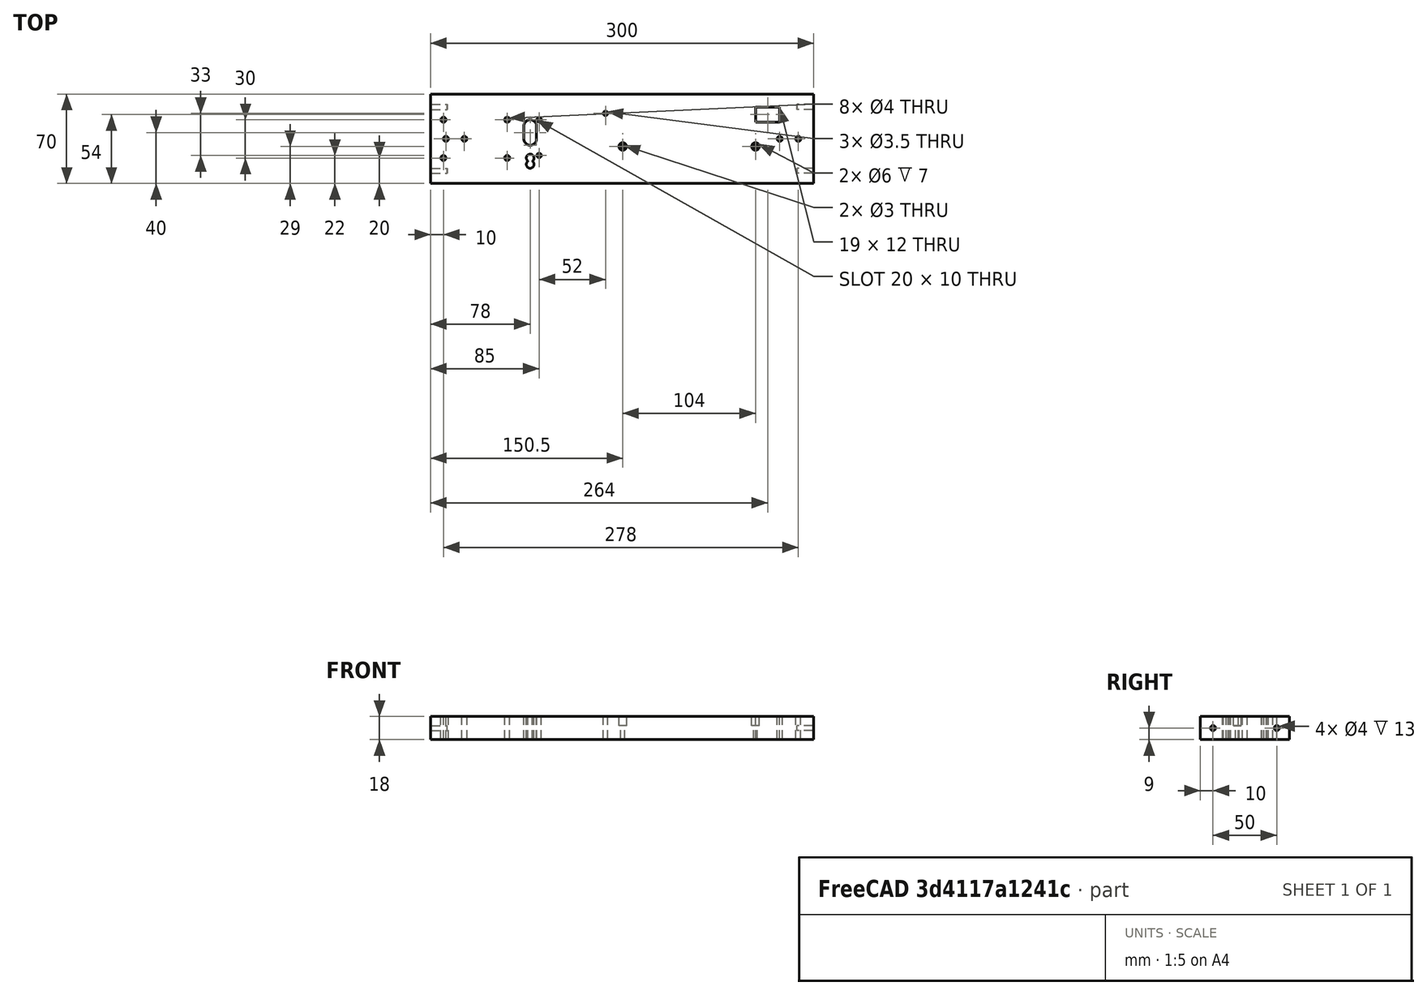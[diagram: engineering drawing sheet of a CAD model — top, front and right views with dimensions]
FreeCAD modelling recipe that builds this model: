
FCSTD DOCUMENT  (FreeCAD 0.17R13541 (Git))
Label: BaseLateralIzquierda
License: All rights reserved
LicenseURL: http://en.wikipedia.org/wiki/All_rights_reserved
objects: Part::Cylinder×21, Part::Cut×13, Part::Box×3, Part::MultiFuse×3, Part::Mirroring×2
note: 42 computed .brp shape members not serialized (recipe doc carries the construction recipe); baked Part::Feature solids carry a one-line shape summary decoded from their .brp

FEATURE [Part::Box] Box  label="Cubo"
  AttacherType = Attacher::AttachEngine3D
  Height = 18
  Length = 300
  Width = 70
FEATURE [Part::Cylinder] Cylinder  label="Cilindro"
  Angle = 360
  AttacherType = Attacher::AttachEngine3D
  Height = 25
  Placement = pos=(10,20,0) rot=(0,0,1;0rad)
  Radius = 2
FEATURE [Part::Cylinder] Cylinder001  label="Cilindro001"
  Angle = 360
  AttacherType = Attacher::AttachEngine3D
  Height = 25
  Placement = pos=(10,50,0) rot=(0,0,1;0rad)
  Radius = 2
FEATURE [Part::Cylinder] Cylinder002  label="Cilindro002"
  Angle = 360
  AttacherType = Attacher::AttachEngine3D
  Height = 25
  Placement = pos=(60,20,0) rot=(0,0,1;0rad)
  Radius = 2
FEATURE [Part::Cylinder] Cylinder003  label="Cilindro003"
  Angle = 360
  AttacherType = Attacher::AttachEngine3D
  Height = 25
  Placement = pos=(60,50,0) rot=(0,0,1;0rad)
  Radius = 2
FEATURE [Part::Cylinder] Cylinder004  label="Cilindro004"
  Angle = 360
  AttacherType = Attacher::AttachEngine3D
  Height = 25
  Placement = pos=(12,35,0) rot=(0,0,1;0rad)
  Radius = 2
FEATURE [Part::Cylinder] Cylinder005  label="Cilindro005"
  Angle = 360
  AttacherType = Attacher::AttachEngine3D
  Height = 25
  Placement = pos=(26.5,35,0) rot=(0,0,1;0rad)
  Radius = 2
FEATURE [Part::Cylinder] Cylinder006  label="Cilindro006"
  Angle = 360
  AttacherType = Attacher::AttachEngine3D
  Height = 25
  Placement = pos=(78,15,0) rot=(0,0,1;0rad)
  Radius = 3
FEATURE [Part::Cylinder] Cylinder007  label="Cilindro007"
  Angle = 360
  AttacherType = Attacher::AttachEngine3D
  Height = 25
  Placement = pos=(78,20,0) rot=(0,0,1;0rad)
  Radius = 3
FEATURE [Part::Cylinder] Cylinder008  label="Cilindro008"
  Angle = 360
  AttacherType = Attacher::AttachEngine3D
  Height = 25
  Placement = pos=(78,35,0) rot=(0,0,1;0rad)
  Radius = 5
FEATURE [Part::Cylinder] Cylinder009  label="Cilindro009"
  Angle = 360
  AttacherType = Attacher::AttachEngine3D
  Height = 25
  Placement = pos=(78,45,0) rot=(0,0,1;0rad)
  Radius = 5
FEATURE [Part::Box] Box001  label="Cubo001"
  AttacherType = Attacher::AttachEngine3D
  Height = 25
  Length = 10
  Placement = pos=(73,35,0) rot=(0,0,1;0rad)
  Width = 10
FEATURE [Part::MultiFuse] Fusion
  Refine = true
  Shapes = -> [Cylinder001,Cylinder002,Cylinder003,Cylinder004,Cylinder005,Cylinder006,Cylinder007,Cylinder008,Cylinder009,Box001,Cylinder]
FEATURE [Part::Cut] Cut
  Base = -> Box
  Refine = true
  Tool = -> Fusion
FEATURE [Part::Cylinder] Cylinder010  label="Cilindro010"
  Angle = 360
  AttacherType = Attacher::AttachEngine3D
  Height = 25
  Placement = pos=(85,22,0) rot=(0,0,1;0rad)
  Radius = 1.75
FEATURE [Part::Cylinder] Cylinder011  label="Cilindro011"
  Angle = 360
  AttacherType = Attacher::AttachEngine3D
  Height = 25
  Placement = pos=(85,50,0) rot=(0,0,1;0rad)
  Radius = 1.75
FEATURE [Part::Cylinder] Cylinder012  label="Cilindro012"
  Angle = 360
  AttacherType = Attacher::AttachEngine3D
  Height = 25
  Placement = pos=(137,55,0) rot=(0,0,1;0rad)
  Radius = 1.75
FEATURE [Part::Cylinder] Cylinder013  label="Cilindro013"
  Angle = 360
  AttacherType = Attacher::AttachEngine3D
  Height = 25
  Placement = pos=(150.5,29,0) rot=(0,0,1;0rad)
  Radius = 1.5
FEATURE [Part::Cylinder] Cylinder014  label="Cilindro014"
  Angle = 360
  AttacherType = Attacher::AttachEngine3D
  Height = 25
  Placement = pos=(150.5,29,11) rot=(0,0,1;0rad)
  Radius = 3
FEATURE [Part::MultiFuse] Fusion001
  Refine = true
  Shapes = -> [Cylinder014,Cylinder013]
FEATURE [Part::Cylinder] Cylinder015  label="Cilindro015"
  Angle = 360
  AttacherType = Attacher::AttachEngine3D
  Height = 25
  Placement = pos=(150.5,29,0) rot=(0,0,1;0rad)
  Radius = 1.5
FEATURE [Part::Cylinder] Cylinder016  label="Cilindro016"
  Angle = 360
  AttacherType = Attacher::AttachEngine3D
  Height = 25
  Placement = pos=(150.5,29,11) rot=(0,0,1;0rad)
  Radius = 3
FEATURE [Part::MultiFuse] Fusion002
  Placement = pos=(104,0,0) rot=(0,0,1;0rad)
  Refine = true
  Shapes = -> [Cylinder016,Cylinder015]
FEATURE [Part::Cut] Cut001
  Base = -> Cut
  Refine = true
  Tool = -> Cylinder010
FEATURE [Part::Cut] Cut002
  Base = -> Cut001
  Refine = true
  Tool = -> Cylinder011
FEATURE [Part::Cut] Cut003
  Base = -> Cut002
  Refine = true
  Tool = -> Cylinder012
FEATURE [Part::Cut] Cut004
  Base = -> Cut003
  Refine = true
  Tool = -> Fusion001
FEATURE [Part::Cut] Cut005
  Base = -> Cut004
  Refine = true
  Tool = -> Fusion002
FEATURE [Part::Cylinder] Cylinder017  label="Cilindro017"
  Angle = 360
  AttacherType = Attacher::AttachEngine3D
  Height = 25
  Placement = pos=(288,35,0) rot=(0,0,1;0rad)
  Radius = 2
FEATURE [Part::Cylinder] Cylinder018  label="Cilindro018"
  Angle = 360
  AttacherType = Attacher::AttachEngine3D
  Height = 25
  Placement = pos=(273.5,35,0) rot=(0,0,1;0rad)
  Radius = 2
FEATURE [Part::Cut] Cut006
  Base = -> Cut005
  Refine = true
  Tool = -> Cylinder018
FEATURE [Part::Cut] Cut007
  Base = -> Cut006
  Refine = true
  Tool = -> Cylinder017
FEATURE [Part::Box] Box002  label="Cubo002"
  AttacherType = Attacher::AttachEngine3D
  Height = 25
  Length = 19
  Placement = pos=(254.5,48,0) rot=(0,0,1;0rad)
  Width = 12
FEATURE [Part::Cut] Cut008
  Base = -> Cut007
  Refine = true
  Tool = -> Box002
FEATURE [Part::Cylinder] Cylinder019  label="Cilindro019"
  Angle = 360
  AttacherType = Attacher::AttachEngine3D
  Height = 13
  Placement = pos=(0,10,9) rot=(0,1,0;1.5708rad)
  Radius = 2
FEATURE [Part::Cylinder] Cylinder020  label="Cilindro020"
  Angle = 360
  AttacherType = Attacher::AttachEngine3D
  Height = 13
  Placement = pos=(0,60,9) rot=(0,1,0;1.5708rad)
  Radius = 2
FEATURE [Part::Mirroring] mirror  label="Mirror of Cilindro019"
  Base = (300,0,18)
  Normal = (0.79,0,0)
  Placement = pos=(-300,0,0) rot=(0,0,1;0rad)
  Source = -> Cylinder019
FEATURE [Part::Mirroring] mirror001  label="Mirror of Cilindro020"
  Base = (300,0,18)
  Normal = (0.790693,0,0)
  Placement = pos=(-300,0,0) rot=(0,0,1;0rad)
  Source = -> Cylinder020
FEATURE [Part::Cut] Cut009
  Base = -> Cut008
  Refine = true
  Tool = -> Cylinder019
FEATURE [Part::Cut] Cut010
  Base = -> Cut009
  Refine = true
  Tool = -> Cylinder020
FEATURE [Part::Cut] Cut011
  Base = -> Cut010
  Refine = true
  Tool = -> mirror
FEATURE [Part::Cut] Cut012
  Base = -> Cut011
  Refine = true
  Tool = -> mirror001
